# Revit family: Faucet-Widespread-American_Standard-Delancey-7052807_Series
name_source: partatom
category: Plumbing Fixtures
units: mm (PartAtom-declared; Revit-internal decimal feet)

## family parameters
Always vertical = No
Cut with Voids When Loaded = No
OmniClass Number = 23.45.55.17
OmniClass Title = Mixing Faucets
Part Type = Normal
Room Calculation Point = No
Round Connector Dimension = Use Diameter
Shared = Yes
Work Plane-Based = Yes

## types (4) — shared parameters
ADA Compliant = Yes
ASME A112.18.1/CSA B125.1 = Yes
Assembly Code = D2020300
CW Connection = Yes
CWFU = 1.5
Cold Water Connection Diameter = 3/8"
Default Elevation = 0"
Description = Delancey Two-Handle Widespread Lavatory Faucet
Faucet Constraint = 8"
Faucet Distance = 8"
Flow Rate = 1.2 gpm (4.5 L/min)
HW Connection = Yes
HWFU = 1.5
Height = 7 3/4"
Hot Water Connection Diameter = 3/8"
Installation Type = Deck Mounted
Manufacturer = American Standard
Pop-Up Drain = Yes
Price = Prices may vary. Please consult Manufacturer Representative for most up-to-date price list.
Product Documentation Link = https://americanstandard.box.com
Product Page URL = https://www.americanstandard-us.com
Revised Date = 09/29/2021
URL = http://www.americanstandard-us.com
Vent Connection = No
WFU = 2
Waste Connection = Yes
Width = 11"

## per-type parameters (varying)
| type | Finish | Handle Type | Material |
| 7052807.002 | Brass-American Standard-002-Polished Chrome | Handle : 002 Lever | Brass-American Standard-002-Polished Chrome |
| 7052807.295 | Brass-American Standard-295-Brushed Nickel | Handle : 295 Lever | Brass-American Standard-295-Brushed Nickel |
| 7052807.013 | Brass-American Standard-013-Polished Nickel | Handle : 013 Lever | Brass-American Standard-013-Polished Nickel |
| 7052807.278 | Brass-American Standard-278-Legacy Bronze | Handle : 278 Lever | Brass-American Standard-278-Legacy Bronze |

note: column(s) folded — value = type name in every type: Model

## geometry (parser evidence)
native form markers: Sweep x5
no freeform markers — native parametric forms only
